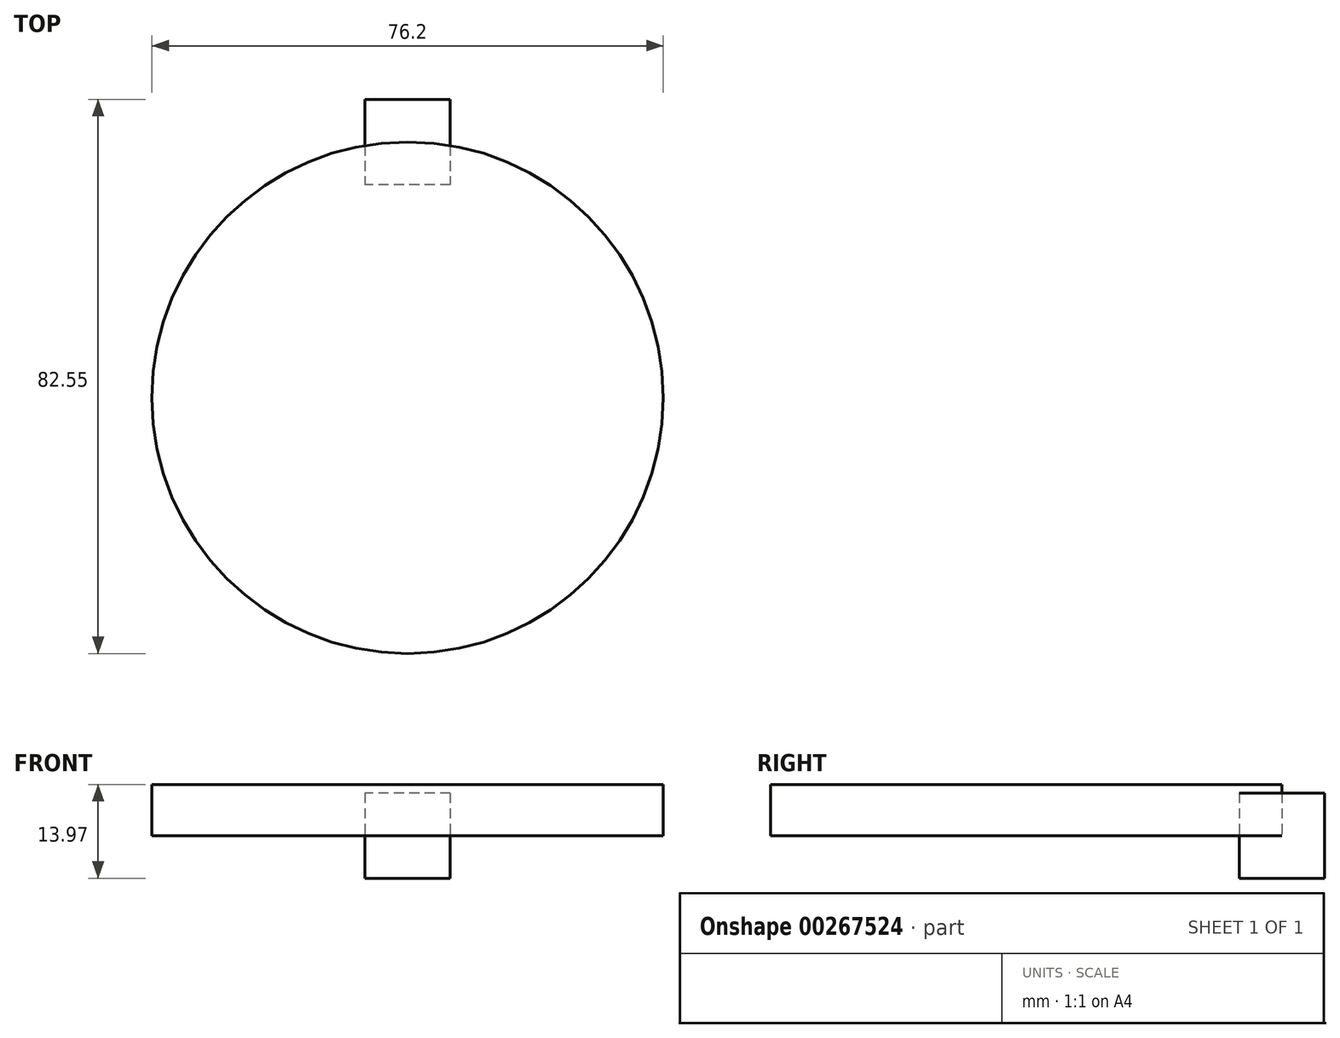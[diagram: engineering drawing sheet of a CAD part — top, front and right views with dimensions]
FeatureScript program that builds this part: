
annotation { "Feature Type Name" : "Feature", "Feature Type Description" : "" }
export const myFeature = defineFeature(function(context is Context, id is Id, definition is map)
    precondition{}
    {
        {
            var Q0;
            Q0=qCreatedBy(makeId("Top.planeOp"),FACE);
            var sketch = newSketch(context, id + "F0", { "sketchPlane" : qUnion([Q0])});
            skCircle(sketch, "E0", {"center": v(0, 0) * mm, "radius": 38.1 * mm});
            skLineSegment(sketch, "E1.bottom", {"start": v(6.35, 44.45) * mm, "end": v(-6.35, 44.45) * mm});
            skLineSegment(sketch, "E1.top", {"start": v(6.35, 31.75) * mm, "end": v(-6.35, 31.75) * mm});
            skLineSegment(sketch, "E1.left", {"start": v(6.35, 44.45) * mm, "end": v(6.35, 31.75) * mm});
            skLineSegment(sketch, "E1.right", {"start": v(-6.35, 44.45) * mm, "end": v(-6.35, 31.75) * mm});
            skPoint(sketch, "E1.middle", {"position": v(0, 38.1) * mm});
            skSolve(sketch);
        }
        {
            var Q0;
            Q0=makeQuery(id+"F0.imprint","IMPRINT",FACE,{"disambiguationData":[TD([[makeQuery(id+"F0.imprint","IMPRINT",EDGE,{"derivedFrom":sQuery(id+"F0.wireOp",EDGE,"E0")}),1.0]])]});
            extrude(context, id + "F1", {"entities" : qUnion([Q0]), "depth" : 7.62 * mm});
        }
        {
            var Q0;
            {var subQ5=sQuery(id+"F0.wireOp",EDGE,"E1.bottom");Q0=makeQuery(id+"F0.imprint","IMPRINT",FACE,{"disambiguationData":[TD([[makeQuery(id+"F0.imprint","IMPRINT",EDGE,{"derivedFrom":subQ5}),1.0]])]});}
            var Q1;
            {var subQ5=sQuery(id+"F0.wireOp",EDGE,"E1.top");Q1=makeQuery(id+"F0.imprint","IMPRINT",FACE,{"disambiguationData":[TD([[makeQuery(id+"F0.imprint","IMPRINT",EDGE,{"derivedFrom":subQ5}),-1.0]])]});}
            extrude(context, id + "F2", {"entities" : qUnion([Q0, Q1]), "endBound" : BoundingType.SYMMETRIC, "depth" : 12.7 * mm});
        }
    });
